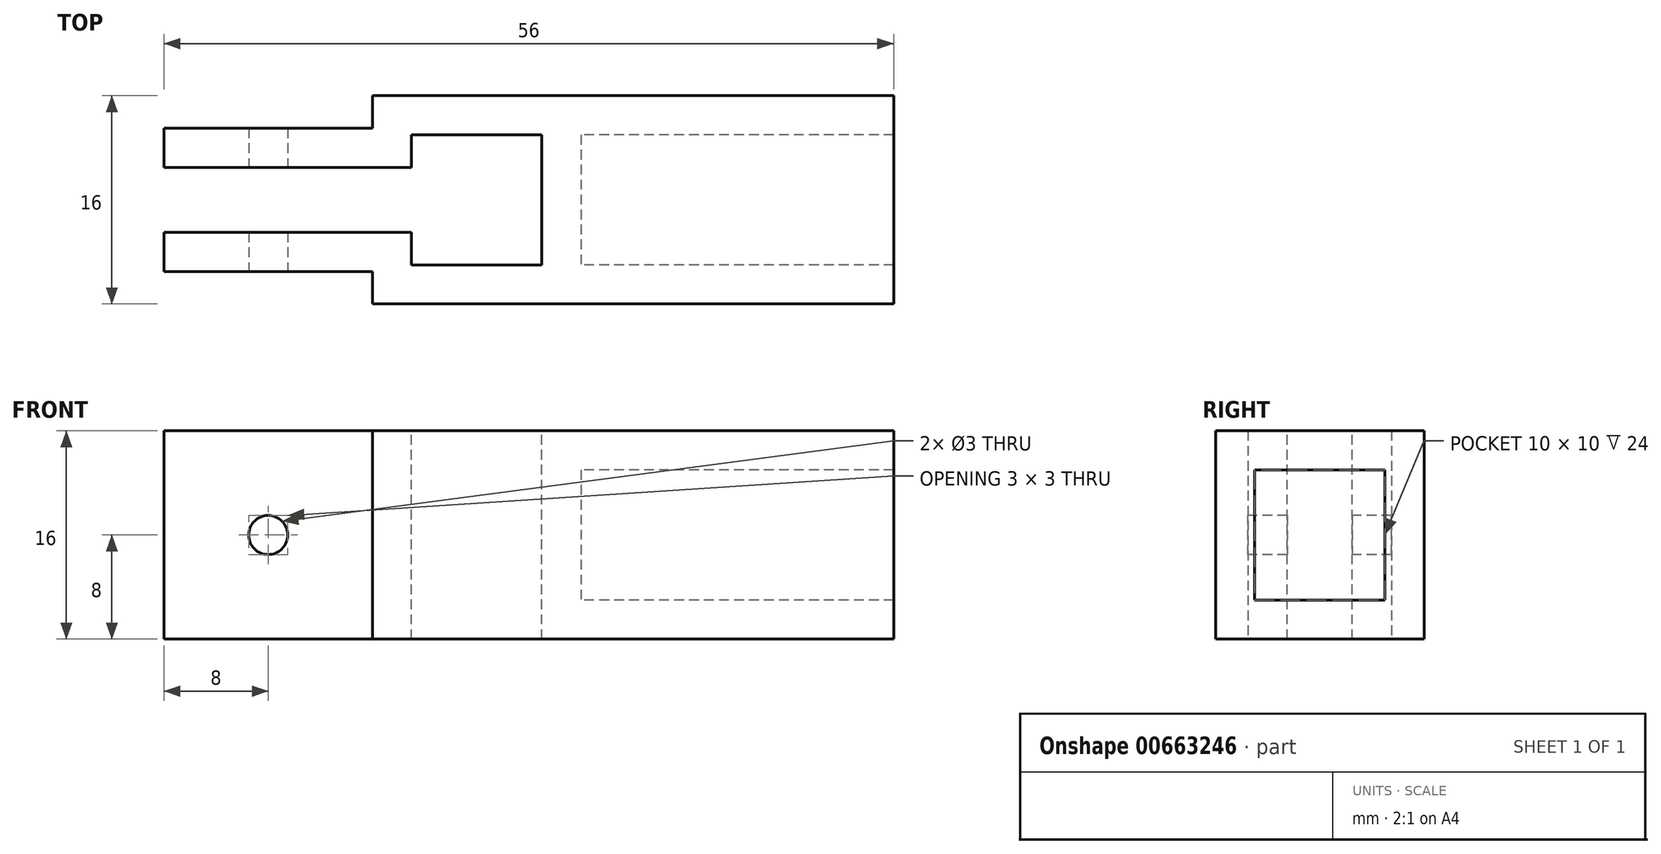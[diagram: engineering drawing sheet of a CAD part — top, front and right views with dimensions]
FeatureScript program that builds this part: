
annotation { "Feature Type Name" : "Feature", "Feature Type Description" : "" }
export const myFeature = defineFeature(function(context is Context, id is Id, definition is map)
    precondition{}
    {
        {
            var Q0;
            Q0=qCreatedBy(makeId("Right.planeOp"),FACE);
            var sketch = newSketch(context, id + "F0", { "sketchPlane" : qUnion([Q0])});
            skLineSegment(sketch, "E0.bottom", {"start": v(8, 8) * mm, "end": v(-8, 8) * mm});
            skLineSegment(sketch, "E0.top", {"start": v(8, -8) * mm, "end": v(-8, -8) * mm});
            skLineSegment(sketch, "E0.left", {"start": v(8, 8) * mm, "end": v(8, -8) * mm});
            skLineSegment(sketch, "E0.right", {"start": v(-8, 8) * mm, "end": v(-8, -8) * mm});
            skPoint(sketch, "E0.middle", {"position": v(0, 0) * mm});
            skLineSegment(sketch, "E1.bottom", {"start": v(5, 5) * mm, "end": v(-5, 5) * mm});
            skLineSegment(sketch, "E1.top", {"start": v(5, -5) * mm, "end": v(-5, -5) * mm});
            skLineSegment(sketch, "E1.left", {"start": v(5, 5) * mm, "end": v(5, -5) * mm});
            skLineSegment(sketch, "E1.right", {"start": v(-5, 5) * mm, "end": v(-5, -5) * mm});
            skSolve(sketch);
        }
        {
            var Q0;
            Q0 = qSketchRegion(id + "F0", true);
            extrude(context, id + "F1", {"entities" : qUnion([Q0]), "depth" : 24 * mm, "offsetDistance" : 25 * mm});
        }
        {
            var Q0;
            Q0=makeQuery(id+"F1.opExtrude","SWEPT_FACE",FACE,{"disambiguationData":[OSD([sQuery(id+"F0.wireOp",EDGE,"E0.bottom")])]});
            var sketch = newSketch(context, id + "F2", { "sketchPlane" : qUnion([Q0])});
            skLineSegment(sketch, "E2.bottom", {"start": v(0, 8) * mm, "end": v(-16, 8) * mm});
            skLineSegment(sketch, "E2.top", {"start": v(0, -8) * mm, "end": v(-16, -8) * mm});
            skLineSegment(sketch, "E2.left", {"start": v(0, 8) * mm, "end": v(0, -8) * mm});
            skLineSegment(sketch, "E2.right", {"start": v(-16, 8) * mm, "end": v(-16, -8) * mm});
            skLineSegment(sketch, "E3.0", {"start": v(-3, 5) * mm, "end": v(-13, 5) * mm});
            skLineSegment(sketch, "E3.1", {"start": v(-3, 5) * mm, "end": v(-3, -5) * mm});
            skLineSegment(sketch, "E3.2", {"start": v(-3, -5) * mm, "end": v(-13, -5) * mm});
            skLineSegment(sketch, "E3.3", {"start": v(-13, 5) * mm, "end": v(-13, -5) * mm});
            skSolve(sketch);
        }
        {
            var Q0;
            Q0 = qSketchRegion(id + "F2", true);
            extrude(context, id + "F3", {"entities" : qUnion([Q0]), "operationType" : NewBodyOperationType.ADD, "oppositeDirection" : true, "depth" : 16 * mm, "offsetDistance" : 25 * mm});
        }
        {
            var Q0;
            Q0=makeQuery(id+"F3.boolean.opBoolean","MERGE",FACE,{"derivedFrom":[makeQuery(id+"F1.opExtrude","SWEPT_FACE",FACE,{"disambiguationData":[OSD([sQuery(id+"F0.wireOp",EDGE,"E0.bottom")])]}),makeQuery(id+"F3.opExtrude","CAP_FACE",FACE,{"disambiguationData":[OSD([sQuery(id+"F2.wireOp",EDGE,"E2.bottom"),sQuery(id+"F2.wireOp",EDGE,"E2.top"),sQuery(id+"F2.wireOp",EDGE,"E2.left"),sQuery(id+"F2.wireOp",EDGE,"E2.right"),sQuery(id+"F2.wireOp",EDGE,"E3.0"),sQuery(id+"F2.wireOp",EDGE,"E3.1"),sQuery(id+"F2.wireOp",EDGE,"E3.2"),sQuery(id+"F2.wireOp",EDGE,"E3.3")])],"isStart":true})]});
            var sketch = newSketch(context, id + "F4", { "sketchPlane" : qUnion([Q0])});
            skLineSegment(sketch, "E4", {"start": v(-16, 0) * mm, "end": v(-13, 0) * mm, "construction": true});
            skLineSegment(sketch, "E5.bottom", {"start": v(-13, 2.5) * mm, "end": v(-16, 2.5) * mm});
            skLineSegment(sketch, "E5.top", {"start": v(-13, -2.5) * mm, "end": v(-16, -2.5) * mm});
            skLineSegment(sketch, "E5.left", {"start": v(-13, 2.5) * mm, "end": v(-13, -2.5) * mm});
            skLineSegment(sketch, "E5.right", {"start": v(-16, 2.5) * mm, "end": v(-16, -2.5) * mm});
            skPoint(sketch, "E5.middle", {"position": v(-14.5, 0) * mm});
            skSolve(sketch);
        }
        {
            var Q0;
            Q0 = qSketchRegion(id + "F4", true);
            extrude(context, id + "F5", {"entities" : qUnion([Q0]), "operationType" : NewBodyOperationType.REMOVE, "oppositeDirection" : true, "depth" : 25 * mm, "offsetDistance" : 25 * mm});
        }
        {
            var Q0;
            {var subQ5=sQuery(id+"F2.wireOp",EDGE,"E2.right");Q0=makeQuery(id+"F5.boolean.opBoolean","SPLIT",FACE,{"disambiguationData":[TD([makeQuery(id+"F1.opExtrude","SWEPT_FACE",FACE,{"disambiguationData":[OSD([sQuery(id+"F0.wireOp",EDGE,"E0.left")])]})])],"derivedFrom":makeQuery(id+"F3.opExtrude","SWEPT_FACE",FACE,{"disambiguationData":[OSD([subQ5])]})});}
            var sketch = newSketch(context, id + "F6", { "sketchPlane" : qUnion([Q0])});
            skLineSegment(sketch, "E6.bottom", {"start": v(-2.5, 8) * mm, "end": v(-5.5, 8) * mm});
            skLineSegment(sketch, "E6.top", {"start": v(-2.5, -8) * mm, "end": v(-5.5, -8) * mm});
            skLineSegment(sketch, "E6.left", {"start": v(-2.5, 8) * mm, "end": v(-2.5, -8) * mm});
            skLineSegment(sketch, "E6.right", {"start": v(-5.5, 8) * mm, "end": v(-5.5, -8) * mm});
            skLineSegment(sketch, "E7.MirrorCS", {"start": v(2.5, 8) * mm, "end": v(2.5, -8) * mm});
            skLineSegment(sketch, "E8.MirrorCS", {"start": v(2.5, 8) * mm, "end": v(5.5, 8) * mm});
            skLineSegment(sketch, "E9.MirrorCS", {"start": v(5.5, 8) * mm, "end": v(5.5, -8) * mm});
            skLineSegment(sketch, "E10.MirrorCS", {"start": v(2.5, -8) * mm, "end": v(5.5, -8) * mm});
            skSolve(sketch);
        }
        {
            var Q0;
            Q0 = qSketchRegion(id + "F6", true);
            extrude(context, id + "F7", {"entities" : qUnion([Q0]), "operationType" : NewBodyOperationType.ADD, "depth" : 16 * mm, "offsetDistance" : 25 * mm});
        }
        {
            var Q0;
            Q0=makeQuery(id+"F7.opExtrude","SWEPT_FACE",FACE,{"disambiguationData":[OSD([sQuery(id+"F6.wireOp",EDGE,"E9.MirrorCS")])]});
            var sketch = newSketch(context, id + "F8", { "sketchPlane" : qUnion([Q0])});
            skLineSegment(sketch, "E11", {"start": v(-32, 0) * mm, "end": v(-16, 0) * mm, "construction": true});
            skCircle(sketch, "E12", {"center": v(-24, 0) * mm, "radius": 1.5 * mm});
            skSolve(sketch);
        }
        {
            var Q0;
            Q0=makeQuery(id+"F8.imprint","IMPRINT",FACE,{"disambiguationData":[TD([[makeQuery(id+"F8.imprint","IMPRINT",EDGE,{"derivedFrom":sQuery(id+"F8.wireOp",EDGE,"E12")}),1.0]])]});
            extrude(context, id + "F9", {"entities" : qUnion([Q0]), "operationType" : NewBodyOperationType.REMOVE, "endBound" : BoundingType.THROUGH_ALL, "oppositeDirection" : true, "depth" : 25 * mm, "offsetDistance" : 25 * mm});
        }
    });
